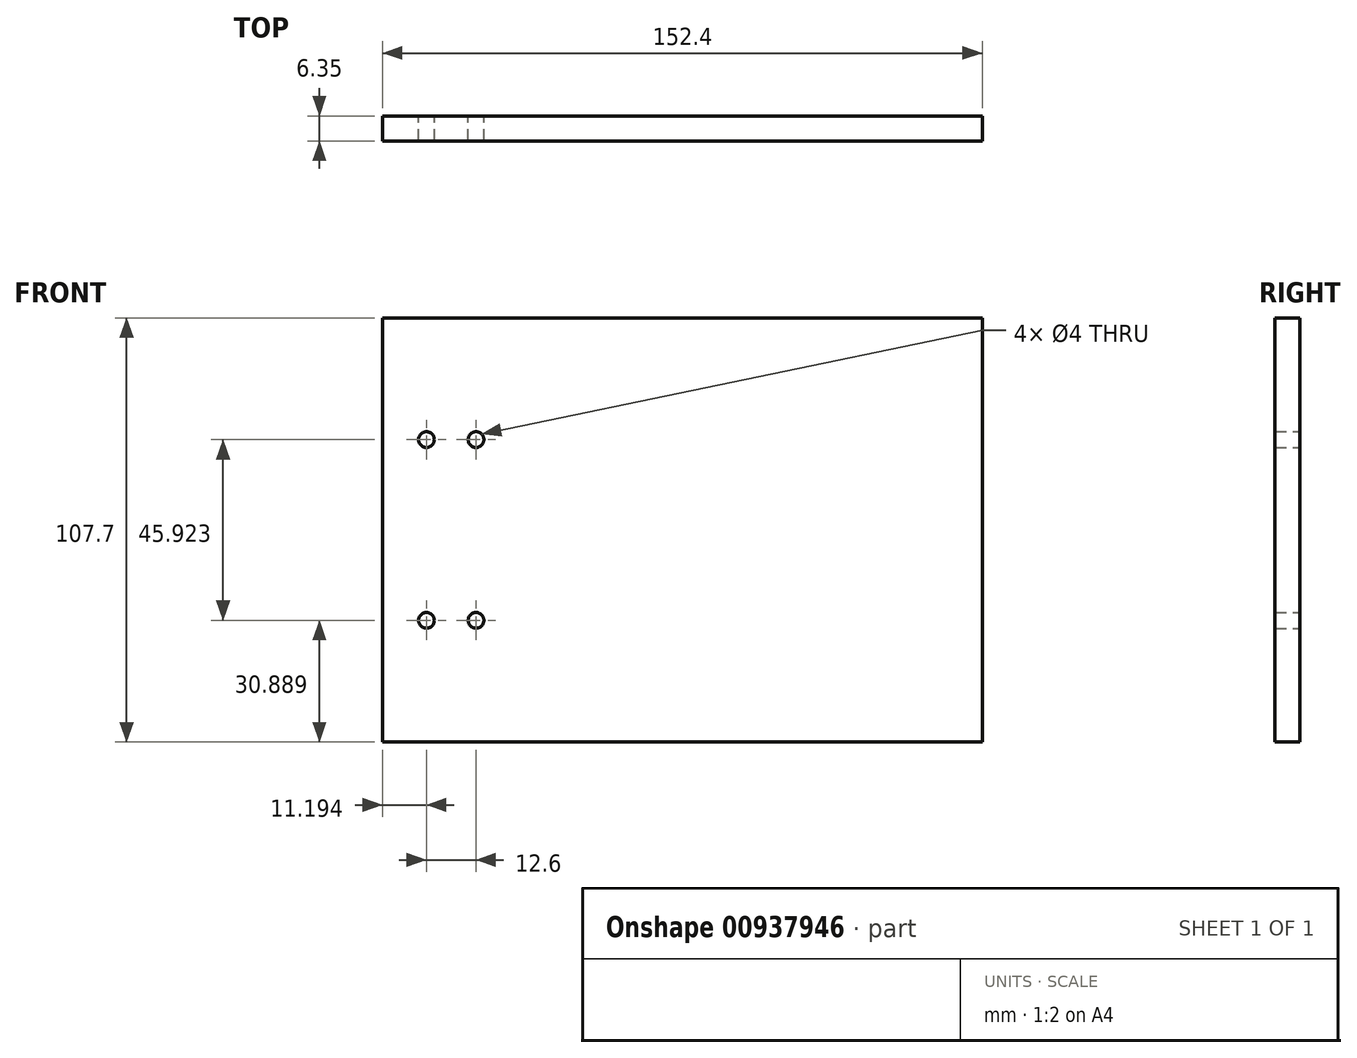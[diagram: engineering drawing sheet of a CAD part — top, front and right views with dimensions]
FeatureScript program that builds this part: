
annotation { "Feature Type Name" : "Feature", "Feature Type Description" : "" }
export const myFeature = defineFeature(function(context is Context, id is Id, definition is map)
    precondition{}
    {
        {
            var Q0;
            Q0=qCreatedBy(makeId("Front.planeOp"),FACE);
            var sketch = newSketch(context, id + "F0", { "sketchPlane" : qUnion([Q0])});
            skLineSegment(sketch, "E0.bottom", {"start": v(-109.6, 102.8) * mm, "end": v(42.8, 102.8) * mm});
            skLineSegment(sketch, "E0.top", {"start": v(-109.6, -4.9) * mm, "end": v(42.8, -4.9) * mm});
            skLineSegment(sketch, "E0.left", {"start": v(-109.6, 102.8) * mm, "end": v(-109.6, -4.9) * mm});
            skLineSegment(sketch, "E0.right", {"start": v(42.8, 102.8) * mm, "end": v(42.8, -4.9) * mm});
            skCircle(sketch, "E1", {"center": v(-98.4, 71.91) * mm, "radius": 2 * mm});
            skCircle(sketch, "E2", {"center": v(-98.4, 25.99) * mm, "radius": 2 * mm});
            skCircle(sketch, "E3", {"center": v(-85.8, 71.91) * mm, "radius": 2 * mm});
            skCircle(sketch, "E4", {"center": v(-85.8, 25.99) * mm, "radius": 2 * mm});
            skLineSegment(sketch, "E5", {"start": v(-98.4, 71.91) * mm, "end": v(-98.4, 25.99) * mm, "construction": true});
            skPoint(sketch, "E6", {"position": v(-98.4, 48.95) * mm});
            skLineSegment(sketch, "E7", {"start": v(-109.6, 48.95) * mm, "end": v(42.8, 48.95) * mm, "construction": true});
            skSolve(sketch);
        }
        {
            var Q0;
            Q0=makeQuery(id+"F0.imprint","IMPRINT",FACE,{"disambiguationData":[TD([[makeQuery(id+"F0.imprint","IMPRINT",EDGE,{"derivedFrom":sQuery(id+"F0.wireOp",EDGE,"E0.bottom")}),-1.0]])]});
            extrude(context, id + "F1", {"entities" : qUnion([Q0]), "depth" : 6.35 * mm, "offsetDistance" : 25.4 * mm});
        }
    });
